# Revit family: Shower-Valve_Trim-KOHLER-Aleo-K-22790IN_1
name_source: partatom
category: Plumbing Fixtures
units: mm (PartAtom-declared; Revit-internal decimal feet)

## family parameters
Cut with Voids When Loaded = No
Host = Face
OmniClass Number = 23.31.25.00
OmniClass Title = Toilet and Bath Specialties
Part Type = Normal
Room Calculation Point = No
Round Connector Dimension = Use Diameter
Shared = No

## types (2) — shared parameters
ADA Compliant = No
Assembly Code = D2010
CW Connection = Yes
Cold Water Inlet = Cold Water Inlet
Date Modified = 02/06/2023
Default Elevation = 42"
Description = Recessed Bath And Shower Trim + At235 In Rose Gold
Drain Included = No
Flow Rate = 0 GPM
HW Connection = Yes
Handle Clearance = 3 7/16"
Height = 6 9/16"
Hot Water Inlet = Hot Water Inlet
Length = 2 11/16"
Manufacturer = Kohler Co.
Master Format 2014 = 22 41 39
Master Format 2014 Name = Residential Showers
Material = Premium Metal Construction
Pressure = 0.00 psi
Product Name = Aleo
Product Page URL = https://www.kohler.co.in
Tempered Water Outlet 1 = Tempered Water Outlet 1
Tempered Water Outlet 2 = Tempered Water Outlet 2
URL = https://www.kohler.co.in
Vent Connection = No
Waste Connection = No
Waste Water Outlet = Waste Water Outlet
WaterSense Certified = No
Width = 4 7/16"

## per-type parameters (varying)
| type | Finish | Model | Type |
| RGD-Polished Rose Gold | Kohler-Metal-RGD-Polished_Rose_Gold | K-22790IN-4-RGD | 1 |
| BV-Brushed Bronze | Kohler-Metal-BV-Brushed_Bronze | K-22790IN-4-BV | 2 |

## geometry (parser evidence)
native form markers: Sweep x5
no freeform markers — native parametric forms only
